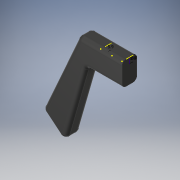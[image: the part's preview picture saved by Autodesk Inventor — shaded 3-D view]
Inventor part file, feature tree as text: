
AUTODESK INVENTOR PART (.ipt)
format: ipt  version: 2018 (Build 220112000, 112)  size: 187,392 bytes
history: native  units: mm
features: sketch x7, extrude x3, fillet x1
ambient origin geometry x8: Origin, YZ Plane, XZ Plane, XY Plane, X Axis, Y Axis, Z Axis, Center Point
bodies: Body1 (feature_tree), Body2 (feature_tree), Body3 (feature_tree)
feature tree (11):
  extrude  "Extrusion3"  Depth=24.0mm
  fillet  "Fillet3"  Radius=24.0mm
  sketch  "Sketch5"  dims[d44=28.8mm d45=4.0mm]
  extrude  "Extrusion4"  Depth=4.0mm
  sketch  "Sketch7"  dims[d49=5.9mm]
  extrude  "Extrusion5"  Depth=4.0mm
  sketch  "Sketch9"  dims[d54=10.0mm d55=0.0mm]
  sketch  "Sketch10"  dims[d56=5.9mm d57=5.9mm]
  sketch  "Sketch4"  dims[d40=22.5mm d41=90.0mm d43=24.0mm]
  sketch  "Sketch6"  dims[d46=15.0mm d47=0.0mm d48=4.0mm]
  sketch  "Sketch8"  dims[d50=11.5mm d51=0.0mm]
